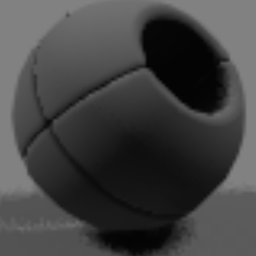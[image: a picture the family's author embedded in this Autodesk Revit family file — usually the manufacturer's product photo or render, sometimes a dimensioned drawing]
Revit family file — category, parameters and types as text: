
# Revit family: 13347CHN_new
name_source: partatom
category: Plumbing Fixtures
units: mm (PartAtom-declared; Revit-internal decimal feet)

## family parameters
Always vertical = No
Cut with Voids When Loaded = No
OmniClass Number = 23.31.11.00
OmniClass Title = Faucets
Part Type = Normal
Room Calculation Point = No
Round Connector Dimension = Use Diameter
Shared = No
Work Plane-Based = Yes

## types (2) — shared parameters
Connector Description = Water Inlet 12.7mm
Default Elevation = 1219 mm
Description = Ecostat Element Bath thermostat for exposed installation
Diameter = 13 mm
Manufacturer = Hansgrohe
Model = 13347CHN
Product Guid = 9b660d7f-bb98-4ab0-8659-a01c3a47c15a
Product Page URL = https://www.hansgrohe.com
Product data url = https://bimobject.com
URL = https://www.hansgrohe.com
Version = 1

## per-type parameters (varying)
| type | Material |
| 007 Chrome | Hansgrohe - Metal - 007 Chrome |
| 677 Matte Black | Hansgrohe - Metal - 677 Matte Black |

## geometry (parser evidence)
native form markers: Sweep x2
no freeform markers — native parametric forms only
